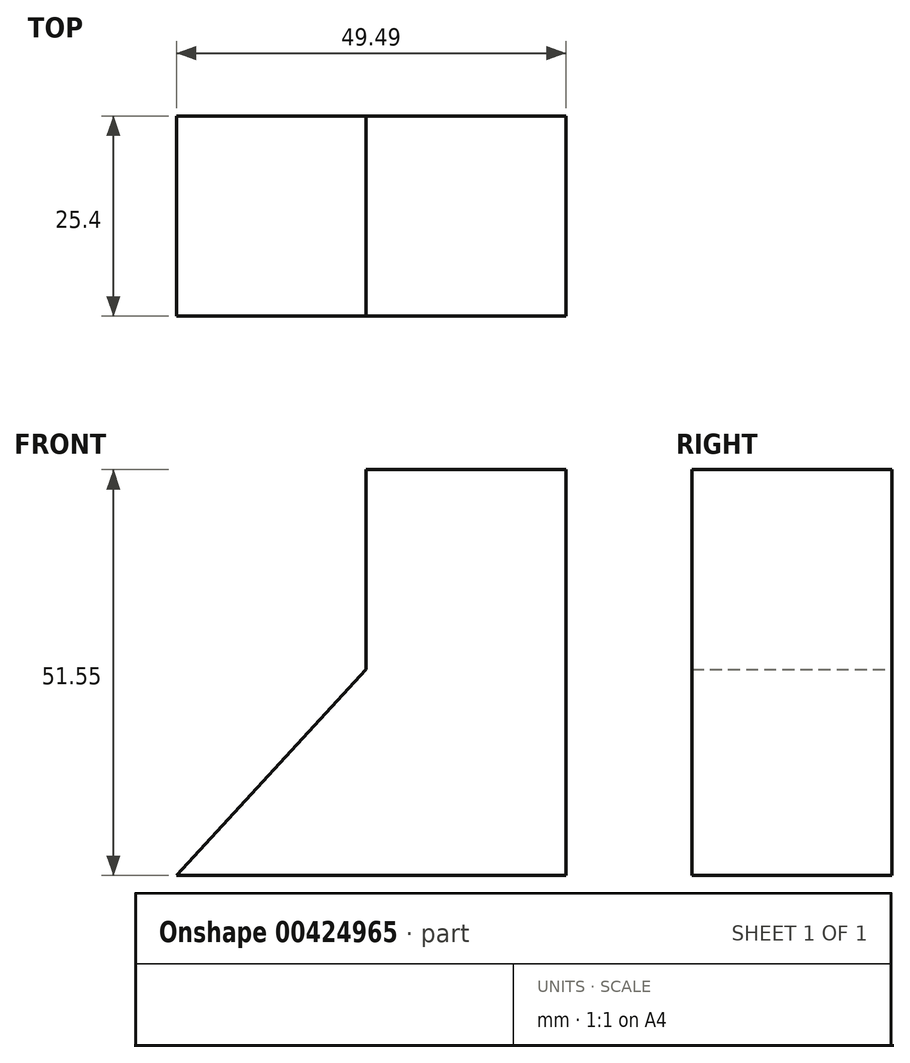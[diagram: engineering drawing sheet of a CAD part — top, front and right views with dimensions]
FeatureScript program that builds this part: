
annotation { "Feature Type Name" : "Feature", "Feature Type Description" : "" }
export const myFeature = defineFeature(function(context is Context, id is Id, definition is map)
    precondition{}
    {
        {
            var Q0;
            Q0=qCreatedBy(makeId("Front.planeOp"),FACE);
            var sketch = newSketch(context, id + "F0", { "sketchPlane" : qUnion([Q0])});
            skLineSegment(sketch, "E0", {"start": v(0, 0) * mm, "end": v(-49.49, 0) * mm});
            skLineSegment(sketch, "E1", {"start": v(0, 0) * mm, "end": v(0, 51.55) * mm});
            skLineSegment(sketch, "E2", {"start": v(0, 51.55) * mm, "end": v(-25.4, 51.55) * mm});
            skLineSegment(sketch, "E3", {"start": v(-25.4, 51.55) * mm, "end": v(-25.4, 26.15) * mm});
            skLineSegment(sketch, "E4", {"start": v(-25.4, 26.15) * mm, "end": v(-49.49, 0) * mm});
            skSolve(sketch);
        }
        {
            var Q0;
            Q0=makeQuery(id+"F0.imprint","IMPRINT",FACE,{"disambiguationData":[TD([[makeQuery(id+"F0.imprint","IMPRINT",EDGE,{"derivedFrom":sQuery(id+"F0.wireOp",EDGE,"E0")}),-1.0]])]});
            extrude(context, id + "F1", {"entities" : qUnion([Q0]), "depth" : 25.4 * mm});
        }
    });
